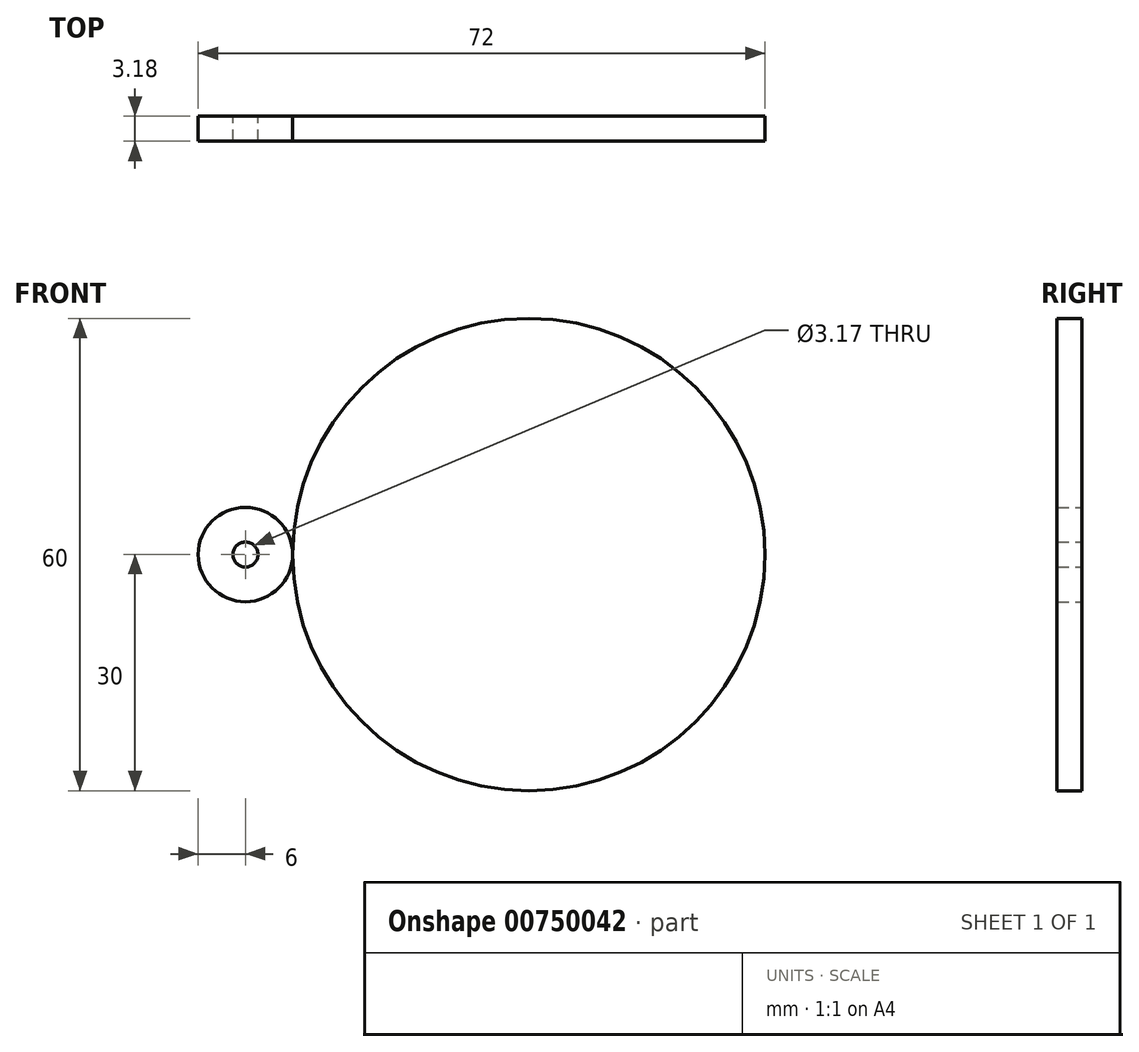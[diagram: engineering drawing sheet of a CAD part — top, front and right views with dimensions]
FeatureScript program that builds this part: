
annotation { "Feature Type Name" : "Feature", "Feature Type Description" : "" }
export const myFeature = defineFeature(function(context is Context, id is Id, definition is map)
    precondition{}
    {
        {
            var Q0;
            Q0=qCreatedBy(makeId("Front.planeOp"),FACE);
            var sketch = newSketch(context, id + "F0", { "sketchPlane" : qUnion([Q0])});
            skCircle(sketch, "E0", {"center": v(0, 0) * mm, "radius": 6 * mm});
            skLineSegment(sketch, "E1", {"start": v(0, 0) * mm, "end": v(36, 0) * mm});
            skCircle(sketch, "E2", {"center": v(36, 0) * mm, "radius": 30 * mm});
            skCircle(sketch, "E3", {"center": v(36, 0) * mm, "radius": 1.59 * mm});
            skSolve(sketch);
        }
        {
            var Q0;
            Q0=makeQuery(id+"F0.imprint","IMPRINT",FACE,{"disambiguationData":[TD([[makeQuery(id+"F0.imprint","IMPRINT",EDGE,{"derivedFrom":sQuery(id+"F0.wireOp",EDGE,"E2")}),1.0]])]});
            var Q1;
            Q1=makeQuery(id+"F0.imprint","IMPRINT",FACE,{"disambiguationData":[TD([[makeQuery(id+"F0.imprint","IMPRINT",EDGE,{"derivedFrom":sQuery(id+"F0.wireOp",EDGE,"E3")}),1.0]])]});
            var Q2;
            Q2=makeQuery(id+"F0.imprint","IMPRINT",FACE,{"disambiguationData":[TD([[makeQuery(id+"F0.imprint","IMPRINT",EDGE,{"derivedFrom":sQuery(id+"F0.wireOp",EDGE,"E0")}),1.0]])]});
            extrude(context, id + "F1", {"entities" : qUnion([Q0, Q1, Q2]), "depth" : 3.17 * mm, "offsetDistance" : 25.4 * mm});
        }
        {
            var Q0;
            Q0=makeQuery(id+"F1.opExtrude","CAP_FACE",FACE,{"disambiguationData":[OSD([sQuery(id+"F0.wireOp",EDGE,"E0")])],"isStart":true});
            var sketch = newSketch(context, id + "F2", { "sketchPlane" : qUnion([Q0])});
            skCircle(sketch, "E4", {"center": v(0, 0) * mm, "radius": 1.59 * mm});
            skSolve(sketch);
        }
        {
            var Q0;
            Q0 = qSketchRegion(id + "F2", true);
            extrude(context, id + "F3", {"entities" : qUnion([Q0]), "operationType" : NewBodyOperationType.REMOVE, "oppositeDirection" : true, "depth" : 25.4 * mm, "offsetDistance" : 25.4 * mm});
        }
    });
